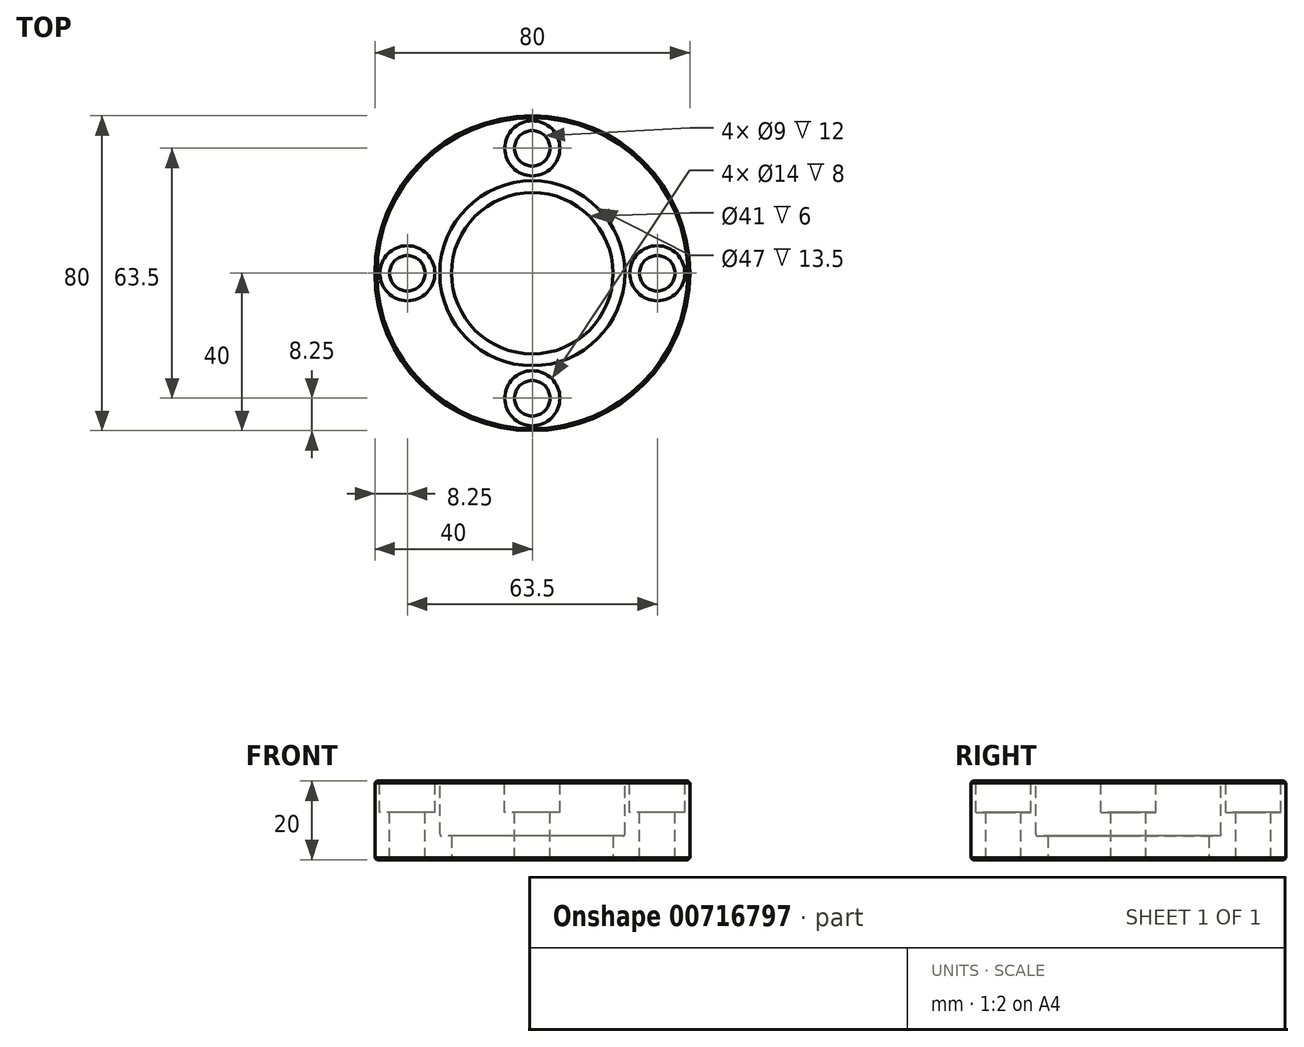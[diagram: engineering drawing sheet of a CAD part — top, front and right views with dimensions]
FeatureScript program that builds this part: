
annotation { "Feature Type Name" : "Feature", "Feature Type Description" : "" }
export const myFeature = defineFeature(function(context is Context, id is Id, definition is map)
    precondition{}
    {
        {
            var Q0;
            Q0=qCreatedBy(makeId("Top.planeOp"),FACE);
            var sketch = newSketch(context, id + "F0", { "sketchPlane" : qUnion([Q0])});
            skCircle(sketch, "E0", {"center": v(0, 0) * mm, "radius": 40 * mm});
            skCircle(sketch, "E1", {"center": v(0, 0) * mm, "radius": 20.5 * mm});
            skSolve(sketch);
        }
        {
            var Q0;
            Q0 = qSketchRegion(id + "F0", true);
            extrude(context, id + "F1", {"entities" : qUnion([Q0]), "endBound" : BoundingType.SYMMETRIC, "depth" : 20 * mm, "offsetDistance" : 25 * mm});
        }
        {
            var Q0;
            Q0=makeQuery(id+"F1.opExtrude","CAP_FACE",FACE,{"disambiguationData":[OSD([sQuery(id+"F0.wireOp",EDGE,"E0"),sQuery(id+"F0.wireOp",EDGE,"E1")])],"isStart":false});
            var sketch = newSketch(context, id + "F2", { "sketchPlane" : qUnion([Q0])});
            skCircle(sketch, "E2", {"center": v(0, 0) * mm, "radius": 23.5 * mm});
            skSolve(sketch);
        }
        {
            var Q0;
            Q0 = qSketchRegion(id + "F2", true);
            extrude(context, id + "F3", {"entities" : qUnion([Q0]), "operationType" : NewBodyOperationType.REMOVE, "oppositeDirection" : true, "depth" : 14 * mm, "offsetDistance" : 25 * mm});
        }
        {
            var Q0;
            Q0=makeQuery(id+"F3.boolean.opBoolean","COPY",EDGE,{"derivedFrom":makeQuery(id+"F3.opExtrude","CAP_EDGE",EDGE,{"disambiguationData":[OSD([sQuery(id+"F2.wireOp",EDGE,"E2")])],"isStart":false})});
            fillet(context, id + "F4", {"entities" : qUnion([Q0]), "radius" : 0.5 * mm, "tangentPropagation" : true, "allowEdgeOverflow" : false});
        }
        {
            var Q0;
            Q0=makeQuery(id+"F3.boolean.opBoolean","COPY",EDGE,{"derivedFrom":makeQuery(id+"F3.opExtrude","CAP_EDGE",EDGE,{"disambiguationData":[OSD([sQuery(id+"F2.wireOp",EDGE,"E2")])],"isStart":true})});
            var Q1;
            Q1=makeQuery(id+"F1.opExtrude","CAP_EDGE",EDGE,{"disambiguationData":[OSD([sQuery(id+"F0.wireOp",EDGE,"E0")])],"isStart":false});
            var Q2;
            Q2=makeQuery(id+"F1.opExtrude","CAP_EDGE",EDGE,{"disambiguationData":[OSD([sQuery(id+"F0.wireOp",EDGE,"E0")])],"isStart":true});
            chamfer(context, id + "F5", {"entities" : qUnion([Q0, Q1, Q2]), "width" : 0.5 * mm, "tangentPropagation" : true});
        }
        {
            var Q0;
            Q0=makeQuery(id+"F1.opExtrude","CAP_FACE",FACE,{"disambiguationData":[OSD([sQuery(id+"F0.wireOp",EDGE,"E0"),sQuery(id+"F0.wireOp",EDGE,"E1")])],"isStart":false});
            var sketch = newSketch(context, id + "F6", { "sketchPlane" : qUnion([Q0])});
            skPoint(sketch, "E3", {"position": v(-31.75, 0) * mm});
            skPoint(sketch, "E4", {"position": v(31.75, 0) * mm});
            skPoint(sketch, "E5", {"position": v(0, 31.75) * mm});
            skPoint(sketch, "E6", {"position": v(0, -31.75) * mm});
            skPoint(sketch, "E7", {"position": v(0, 0) * mm});
            skLineSegment(sketch, "E8", {"start": v(-31.75, 0) * mm, "end": v(31.75, 0) * mm});
            skLineSegment(sketch, "E9", {"start": v(0, 31.75) * mm, "end": v(0, -31.75) * mm});
            skSolve(sketch);
        }
        {
            var Q0;
            Q0=sQuery(id+"F6.wireOp",VERTEX,"E5");
            var Q1;
            Q1=sQuery(id+"F6.wireOp",VERTEX,"E6");
            var Q2;
            Q2=sQuery(id+"F6.wireOp",VERTEX,"E4");
            var Q3;
            Q3=sQuery(id+"F6.wireOp",VERTEX,"E3");
            var Q4;
            Q4=makeQuery(id+"F1.opExtrude","SWEPT_BODY",BODY,{"disambiguationData":[OSD([sQuery(id+"F0.wireOp",EDGE,"E0"),sQuery(id+"F0.wireOp",EDGE,"E1")])]});
            hole(context, id + "F7", {"style" : HoleStyle.C_BORE, "endStyle" : HoleEndStyle.THROUGH, "holeDiameter" : 9 * mm, "cBoreDiameter" : 14 * mm, "cBoreDepth" : 8 * mm, "majorDiameter" : 8 * mm, "isTappedThrough" : true, "tappedDepth" : 12 * mm, "tapClearance" : 3, "startFromSketch" : true, "locations" : qUnion([Q0, Q1, Q2, Q3]), "scope" : qUnion([Q4])});
        }
    });
